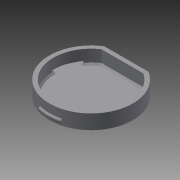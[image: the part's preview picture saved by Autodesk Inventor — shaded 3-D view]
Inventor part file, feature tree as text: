
AUTODESK INVENTOR PART (.ipt)
format: ipt  version: 2015 (Build 190159000, 159)  size: 240,128 bytes
history: native  units: in
note: dims shown in document units (in); Inventor stores cm internally (conversion verified against a paired STEP export)
features: sketch x9, other x8, plane x5, extrude x5, revolve x2, chamfer x2, fillet x1
ambient origin geometry x8: Origin, YZ Plane, XZ Plane, XY Plane, X Axis, Y Axis, Z Axis, Center Point
bodies: Body1 (feature_tree)
feature tree (32):
  revolve  "Revolution1"  [1 undecoded]
  other  "Work Axis1"
  sketch  "Sketch3"  dims[d5=1.5in d6=0.75in]
  other  "Work Point1"
  plane  "Work Plane1"
  extrude  "Extrusion9"  Depth=0.75in
  extrude  "Extrusion10"  Depth=0.65in
  extrude  "Extrusion11"  Depth=0.445in
  plane  "Work Plane8"
  sketch  "Sketch19"  dims[d43=1.05in d54=0.65in]
  plane  "Work Plane9"
  other  "Work Point4"
  other  "Work Point5"
  extrude  "Extrusion16"  Depth=0.65in
  sketch  "Sketch21"  dims[d70=2.0in d71=0.0in d72=0.05in d73=0.17in d74=0.0in]
  sketch  "Sketch22"  dims[d75=2.0in]
  other  "Work Point6"
  other  "Work Axis6"
  plane  "Work Plane10"
  sketch  "Sketch23"  dims[d104=0.2405in d105=0.1202in d106=1.05in d107=0.3171in d108=0.04in d109=0.04in d110=0.15in d111=0.0in d112=0.22in d113=0.47in d114=0.2337in d115=0.05in d122=0.05in d124=0.05in d127=0.05in d130=0.018in d131=0.3in d132=0.0in d133=0.018in d134=0.0264in d135=0.05in d136=30.0deg d137=0.01in d138=0.02in d139=0.125in d140=45.0deg d141=0.03in d142=0.125in d143=45.0deg]
  extrude  "Extrusion19"  Depth=0.22in
  revolve  "Revolution8"  [1 undecoded]
  fillet  "Fillet3"  Radius=0.17in
  chamfer  "Chamfer1"  Distance=0.1202in
  chamfer  "Chamfer2"  Distance=1.05in
  sketch  "Sketch2"  dims[d3=1.5in d4=0.4375in]
  sketch  "Sketch15"  dims[d8=0.45in d9=0.65in]
  sketch  "Sketch16"  dims[d15=90.0deg d42=0.445in]
  plane  "Work Plane7"
  other  "Work Point2"
  other  "Work Point3"
  sketch  "Sketch20"  dims[d67=1.0in d68=0.0in d69=0.22in]
note: 2 required parameter values undecoded (feature->parameter linkage not recoverable at this tier; creation-order binding heuristic only, values carry confidence <= 0.55)
